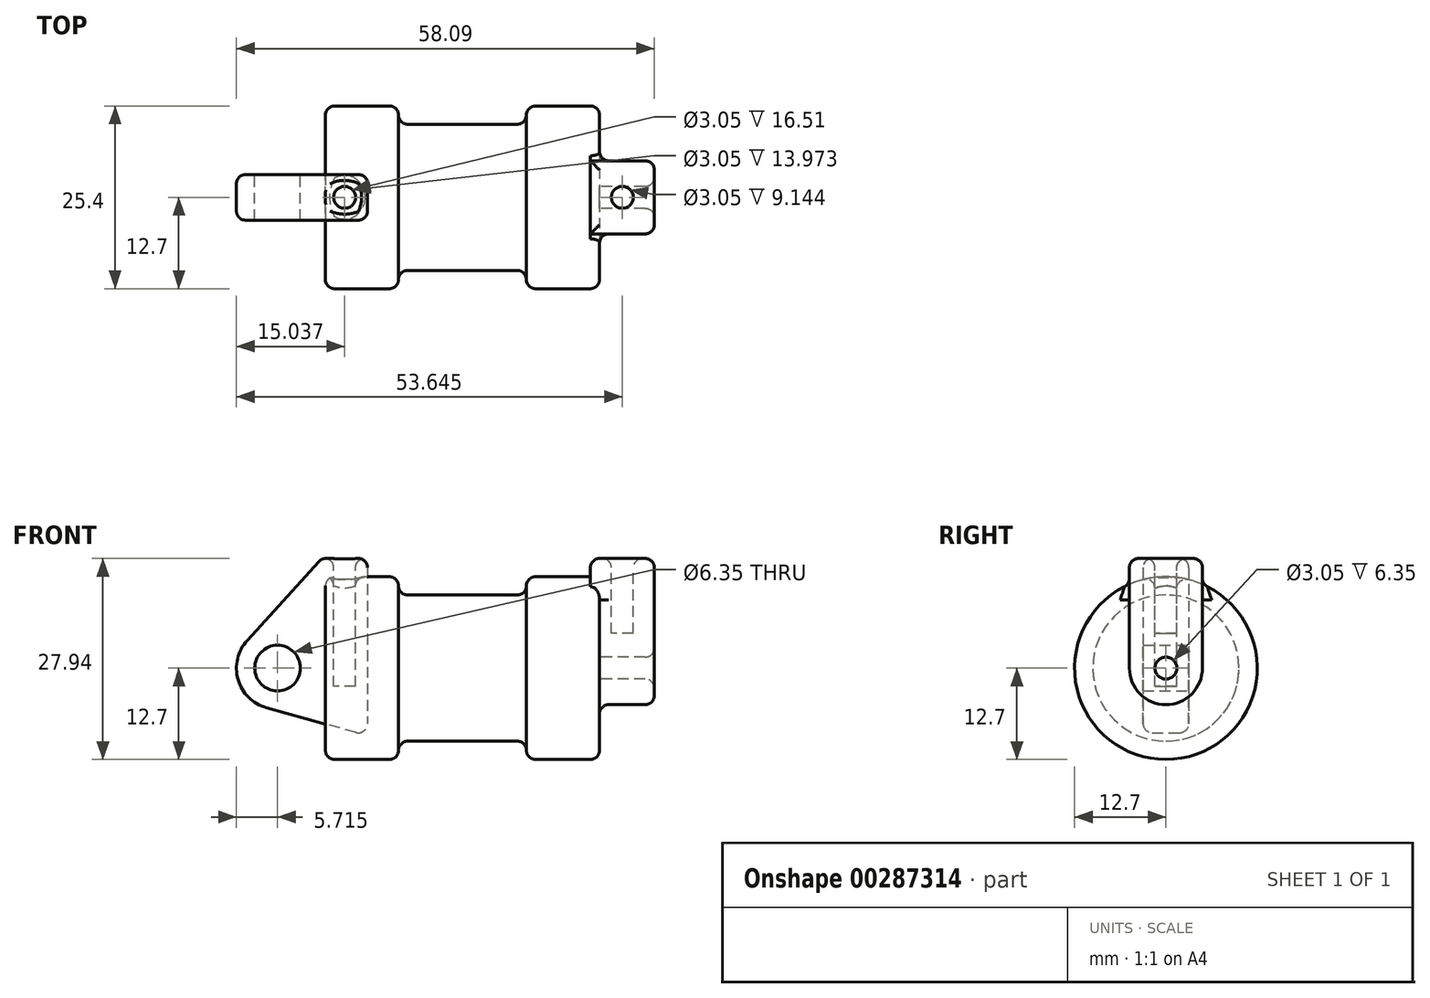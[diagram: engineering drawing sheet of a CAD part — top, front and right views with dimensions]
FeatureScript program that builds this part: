
annotation { "Feature Type Name" : "Feature", "Feature Type Description" : "" }
export const myFeature = defineFeature(function(context is Context, id is Id, definition is map)
    precondition{}
    {
        {
            var Q0;
            Q0=qCreatedBy(makeId("Front.planeOp"),FACE);
            var sketch = newSketch(context, id + "F0", { "sketchPlane" : qUnion([Q0])});
            skLineSegment(sketch, "E0", {"start": v(0, 0) * mm, "end": v(0, 12.7) * mm});
            skLineSegment(sketch, "E1", {"start": v(0, 12.7) * mm, "end": v(10.16, 12.7) * mm});
            skLineSegment(sketch, "E2", {"start": v(10.16, 12.7) * mm, "end": v(10.16, 10.16) * mm});
            skLineSegment(sketch, "E3", {"start": v(10.16, 10.16) * mm, "end": v(27.94, 10.16) * mm});
            skLineSegment(sketch, "E4", {"start": v(27.94, 10.16) * mm, "end": v(27.94, 12.7) * mm});
            skLineSegment(sketch, "E5", {"start": v(27.94, 12.7) * mm, "end": v(38.1, 12.7) * mm});
            skLineSegment(sketch, "E6", {"start": v(38.1, 12.7) * mm, "end": v(38.1, 0) * mm});
            skLineSegment(sketch, "E7", {"start": v(38.1, 0) * mm, "end": v(0, 0) * mm});
            skLineSegment(sketch, "E8", {"start": v(5.84, 15.24) * mm, "end": v(-0.5, 15.24) * mm});
            skLineSegment(sketch, "E9", {"start": v(-0.5, 15.24) * mm, "end": v(-10.88, 3.85) * mm});
            skLineSegment(sketch, "E10", {"start": v(0, 0) * mm, "end": v(-6.65, 0) * mm});
            skCircle(sketch, "E11", {"center": v(-6.65, 0) * mm, "radius": 5.72 * mm});
            skCircle(sketch, "E12", {"center": v(-6.65, 0) * mm, "radius": 3.18 * mm});
            skLineSegment(sketch, "E13", {"start": v(5.84, 15.24) * mm, "end": v(5.84, -9.4) * mm});
            skLineSegment(sketch, "E14", {"start": v(5.84, -9.4) * mm, "end": v(-8.18, -5.5) * mm});
            skSolve(sketch);
        }
        {
            var Q0;
            {var subQ0=sQuery(id+"F0.wireOp",EDGE,"E2");Q0=makeQuery(id+"F0.imprint","IMPRINT",FACE,{"disambiguationData":[TD([[makeQuery(id+"F0.imprint","IMPRINT",EDGE,{"derivedFrom":subQ0}),-1.0]])]});}
            var Q1;
            {var subQ0=sQuery(id+"F0.wireOp",EDGE,"E0");Q1=makeQuery(id+"F0.imprint","IMPRINT",FACE,{"disambiguationData":[TD([[makeQuery(id+"F0.imprint","IMPRINT",EDGE,{"derivedFrom":subQ0}),-1.0]])]});}
            var Q2;
            Q2=sQuery(id+"F0.wireOp",EDGE,"E7");
            revolve(context, id + "F1", {"entities" : qUnion([Q0, Q1]), "axis" : qUnion([Q2]), "revolveType" : RevolveType.FULL});
        }
        {
            var Q0;
            {var subQ0=sQuery(id+"F0.wireOp",EDGE,"E0");Q0=makeQuery(id+"F0.imprint","IMPRINT",FACE,{"disambiguationData":[TD([[makeQuery(id+"F0.imprint","IMPRINT",EDGE,{"derivedFrom":subQ0}),-1.0]])]});}
            var Q1;
            {var subQ1=sQuery(id+"F0.wireOp",EDGE,"E0");Q1=makeQuery(id+"F0.imprint","IMPRINT",FACE,{"disambiguationData":[TD([[makeQuery(id+"F0.imprint","IMPRINT",EDGE,{"derivedFrom":subQ1}),1.0]])]});}
            var Q2;
            {var subQ5=sQuery(id+"F0.wireOp",EDGE,"E12");Q2=makeQuery(id+"F0.imprint","IMPRINT",FACE,{"disambiguationData":[TD([[makeQuery(id+"F0.imprint","IMPRINT",EDGE,{"derivedFrom":subQ5}),-1.0]])]});}
            var Q3;
            {var subQ0=sQuery(id+"F0.wireOp",EDGE,"E14");Q3=makeQuery(id+"F0.imprint","IMPRINT",FACE,{"disambiguationData":[TD([[makeQuery(id+"F0.imprint","IMPRINT",EDGE,{"derivedFrom":subQ0}),-1.0]])]});}
            extrude(context, id + "F2", {"entities" : qUnion([Q0, Q1, Q2, Q3]), "endBound" : BoundingType.SYMMETRIC, "depth" : 6.35 * mm});
        }
        {
            var Q0;
            Q0=makeQuery(id+"F1.opRevolve","SWEPT_FACE",FACE,{"disambiguationData":[OSD([sQuery(id+"F0.wireOp",EDGE,"E6")])]});
            var sketch = newSketch(context, id + "F3", { "sketchPlane" : qUnion([Q0])});
            skCircle(sketch, "E15", {"center": v(0, 0) * mm, "radius": 1.52 * mm});
            skCircle(sketch, "E16", {"center": v(0, 0) * mm, "radius": 5.08 * mm});
            skLineSegment(sketch, "E17", {"start": v(-5.08, 15.24) * mm, "end": v(-5.08, 0) * mm});
            skLineSegment(sketch, "E18", {"start": v(5.08, 15.24) * mm, "end": v(5.08, 0) * mm});
            skLineSegment(sketch, "E19", {"start": v(-5.08, 15.24) * mm, "end": v(5.08, 15.24) * mm});
            skSolve(sketch);
        }
        {
            var Q0;
            {var subQ0=sQuery(id+"F3.wireOp",EDGE,"E19");Q0=makeQuery(id+"F3.imprint","IMPRINT",FACE,{"disambiguationData":[TD([[makeQuery(id+"F3.imprint","IMPRINT",EDGE,{"derivedFrom":subQ0}),-1.0]])]});}
            var Q1;
            {var subQ0=sQuery(id+"F3.wireOp",EDGE,"E17");var subQ1=sQuery(id+"F3.wireOp",EDGE,"E16");var subQ2=makeQuery(id+"F3.imprint","INTERSECT",VERTEX,{"derivedFrom":[subQ1,subQ0]});Q1=makeQuery(id+"F3.imprint","IMPRINT",FACE,{"disambiguationData":[TD([[makeQuery(id+"F3.imprint","IMPRINT",EDGE,{"disambiguationData":[TD([[subQ2,1.0]])],"derivedFrom":subQ1}),-1.0]])]});}
            var Q2;
            Q2=makeQuery(id+"F3.imprint","IMPRINT",FACE,{"disambiguationData":[TD([[makeQuery(id+"F3.imprint","IMPRINT",EDGE,{"derivedFrom":sQuery(id+"F3.wireOp",EDGE,"E15")}),-1.0]])]});
            extrude(context, id + "F4", {"entities" : qUnion([Q0, Q1, Q2]), "operationType" : NewBodyOperationType.ADD, "depth" : 7.62 * mm});
        }
        {
            var Q0;
            {var subQ0=sQuery(id+"F3.wireOp",EDGE,"E19");Q0=makeQuery(id+"F3.imprint","IMPRINT",FACE,{"disambiguationData":[TD([[makeQuery(id+"F3.imprint","IMPRINT",EDGE,{"derivedFrom":subQ0}),-1.0]])]});}
            extrude(context, id + "F5", {"entities" : qUnion([Q0]), "operationType" : NewBodyOperationType.ADD, "oppositeDirection" : true, "depth" : 1.27 * mm});
        }
        {
            var Q0;
            Q0=makeQuery(id+"F3.imprint","IMPRINT",FACE,{"disambiguationData":[TD([[makeQuery(id+"F3.imprint","IMPRINT",EDGE,{"derivedFrom":sQuery(id+"F3.wireOp",EDGE,"E15")}),1.0]])]});
            var Q1;
            Q1=makeQuery(id+"F4.opExtrude","CAP_FACE",FACE,{"disambiguationData":[OSD([sQuery(id+"F3.wireOp",EDGE,"E15"),sQuery(id+"F3.wireOp",EDGE,"E16"),sQuery(id+"F3.wireOp",EDGE,"E17"),sQuery(id+"F3.wireOp",EDGE,"E18"),sQuery(id+"F3.wireOp",EDGE,"E19")])],"isStart":false});
            extrude(context, id + "F6", {"entities" : qUnion([Q0]), "operationType" : NewBodyOperationType.REMOVE, "endBound" : BoundingType.UP_TO_SURFACE, "endBoundEntityFace" : qUnion([Q1]), "depth" : 25.4 * mm});
        }
        {
            var Q0;
            Q0=makeQuery(id+"F2.opExtrude","SWEPT_FACE",FACE,{"disambiguationData":[OSD([sQuery(id+"F0.wireOp",EDGE,"E8")])]});
            var sketch = newSketch(context, id + "F7", { "sketchPlane" : qUnion([Q0])});
            skCircle(sketch, "E20", {"center": v(2.67, 0) * mm, "radius": 1.52 * mm});
            skSolve(sketch);
        }
        {
            var Q0;
            {var subQ0=sQuery(id+"F3.wireOp",EDGE,"E19");Q0=makeQuery(id+"F5.boolean.opBoolean","MERGE",FACE,{"derivedFrom":[makeQuery(id+"F4.opExtrude","SWEPT_FACE",FACE,{"disambiguationData":[OSD([subQ0])]}),makeQuery(id+"F5.opExtrude","SWEPT_FACE",FACE,{"disambiguationData":[OSD([subQ0])]})]});}
            var sketch = newSketch(context, id + "F8", { "sketchPlane" : qUnion([Q0])});
            skCircle(sketch, "E21", {"center": v(41.28, 0) * mm, "radius": 1.52 * mm});
            skSolve(sketch);
        }
        {
            var Q0;
            Q0=makeQuery(id+"F7.imprint","IMPRINT",FACE,{"disambiguationData":[TD([[makeQuery(id+"F7.imprint","IMPRINT",EDGE,{"derivedFrom":sQuery(id+"F7.wireOp",EDGE,"E20")}),1.0]])]});
            extrude(context, id + "F9", {"entities" : qUnion([Q0]), "operationType" : NewBodyOperationType.REMOVE, "oppositeDirection" : true, "depth" : 17.78 * mm});
        }
        {
            var Q0;
            Q0=makeQuery(id+"F8.imprint","IMPRINT",FACE,{"disambiguationData":[TD([[makeQuery(id+"F8.imprint","IMPRINT",EDGE,{"derivedFrom":sQuery(id+"F8.wireOp",EDGE,"E21")}),1.0]])]});
            extrude(context, id + "F10", {"entities" : qUnion([Q0]), "operationType" : NewBodyOperationType.REMOVE, "oppositeDirection" : true, "depth" : 10.4 * mm});
        }
        {
            var Q0;
            Q0=makeQuery(id+"F1.opRevolve","SWEPT_FACE",FACE,{"disambiguationData":[OSD([sQuery(id+"F0.wireOp",EDGE,"E2")])]});
            var Q1;
            Q1=makeQuery(id+"F2.opExtrude","SWEPT_FACE",FACE,{"disambiguationData":[OSD([sQuery(id+"F0.wireOp",EDGE,"E13")])]});
            var Q2;
            Q2=makeQuery(id+"F1.opRevolve","SWEPT_FACE",FACE,{"disambiguationData":[OSD([sQuery(id+"F0.wireOp",EDGE,"E1")])]});
            var Q3;
            {var subQ0=sQuery(id+"F3.wireOp",EDGE,"E19");Q3=makeQuery(id+"F5.boolean.opBoolean","MERGE",FACE,{"derivedFrom":[makeQuery(id+"F4.opExtrude","SWEPT_FACE",FACE,{"disambiguationData":[OSD([subQ0])]}),makeQuery(id+"F5.opExtrude","SWEPT_FACE",FACE,{"disambiguationData":[OSD([subQ0])]})]});}
            var Q4;
            Q4=makeQuery(id+"F1.opRevolve","SWEPT_FACE",FACE,{"disambiguationData":[OSD([sQuery(id+"F0.wireOp",EDGE,"E4")])]});
            var Q5;
            Q5=makeQuery(id+"F2.opExtrude","SWEPT_FACE",FACE,{"disambiguationData":[OSD([sQuery(id+"F0.wireOp",EDGE,"E9")])]});
            var Q6;
            Q6=makeQuery(id+"F4.boolean.opBoolean","SPLIT",FACE,{"disambiguationData":[TD([makeQuery(id+"F1.opRevolve","SWEPT_FACE",FACE,{"disambiguationData":[OSD([sQuery(id+"F0.wireOp",EDGE,"E5")])]})])],"derivedFrom":makeQuery(id+"F1.opRevolve","SWEPT_FACE",FACE,{"disambiguationData":[OSD([sQuery(id+"F0.wireOp",EDGE,"E6")])]})});
            var Q7;
            Q7=makeQuery(id+"F2.opExtrude","CAP_EDGE",EDGE,{"disambiguationData":[OSD([sQuery(id+"F0.wireOp",EDGE,"E8")])],"isStart":false});
            var Q8;
            Q8=makeQuery(id+"F4.opExtrude","CAP_FACE",FACE,{"disambiguationData":[OSD([sQuery(id+"F3.wireOp",EDGE,"E15"),sQuery(id+"F3.wireOp",EDGE,"E16"),sQuery(id+"F3.wireOp",EDGE,"E17"),sQuery(id+"F3.wireOp",EDGE,"E18"),sQuery(id+"F3.wireOp",EDGE,"E19")])],"isStart":false});
            var Q9;
            Q9=makeQuery(id+"F2.opExtrude","SWEPT_FACE",FACE,{"disambiguationData":[OSD([sQuery(id+"F0.wireOp",EDGE,"E8")])]});
            fillet(context, id + "F11", {"entities" : qUnion([Q0, Q1, Q2, Q3, Q4, Q5, Q6, Q7, Q8, Q9]), "radius" : 1.27 * mm, "tangentPropagation" : true, "allowEdgeOverflow" : false});
        }
    });
